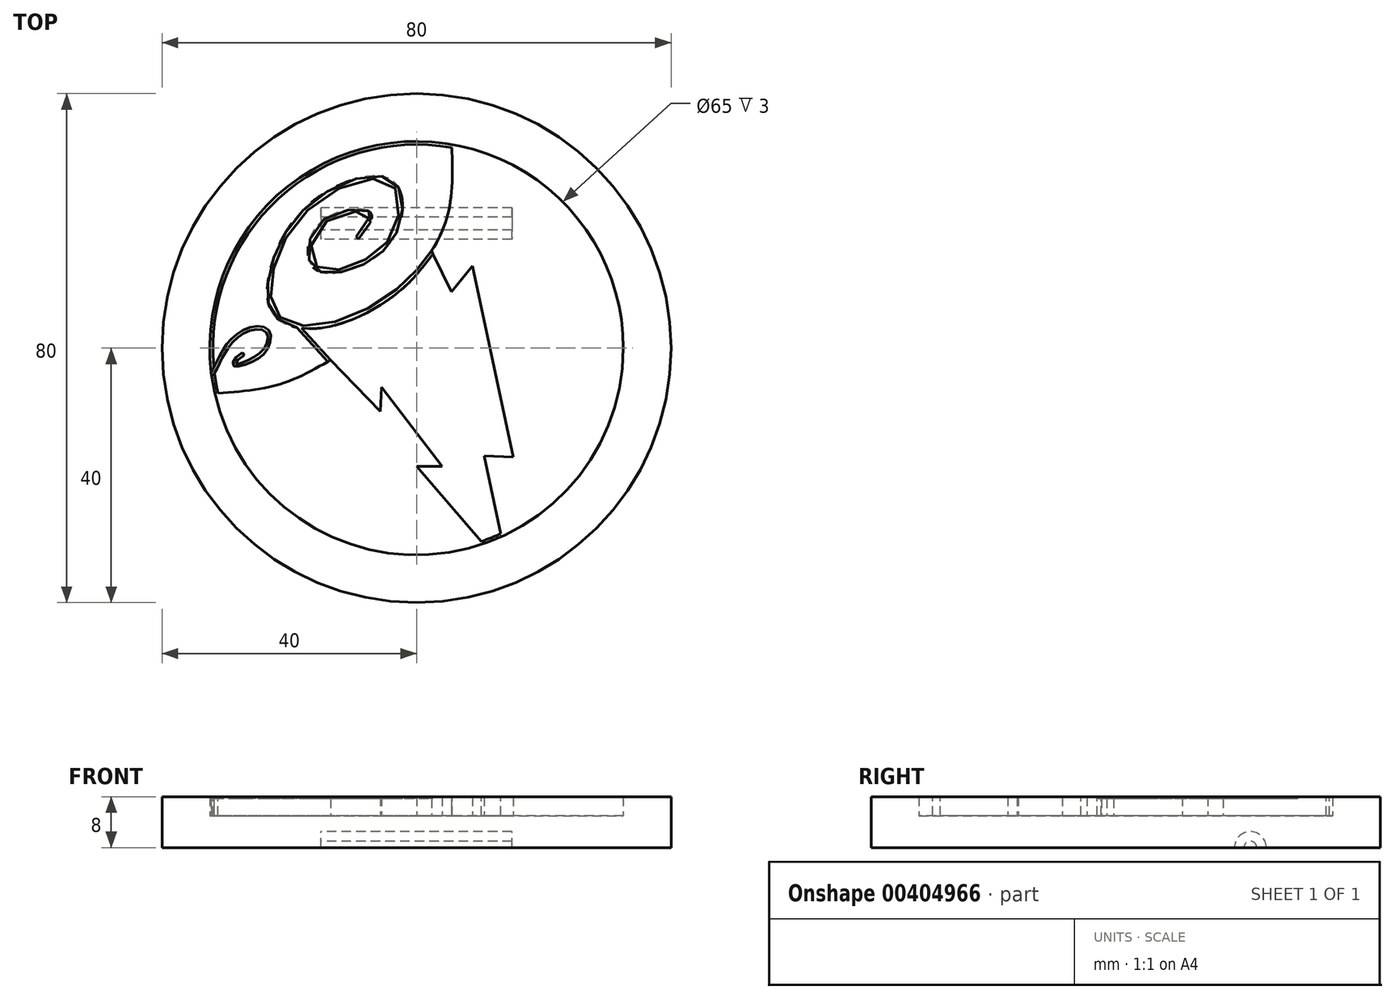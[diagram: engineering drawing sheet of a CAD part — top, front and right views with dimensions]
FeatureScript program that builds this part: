
annotation { "Feature Type Name" : "Feature", "Feature Type Description" : "" }
export const myFeature = defineFeature(function(context is Context, id is Id, definition is map)
    precondition{}
    {
        {
            var Q0;
            Q0=qCreatedBy(makeId("Top.planeOp"),FACE);
            var sketch = newSketch(context, id + "F0", { "sketchPlane" : qUnion([Q0])});
            skCircle(sketch, "E0", {"center": v(0, 0) * mm, "radius": 40 * mm});
            skSolve(sketch);
        }
        {
            var Q0;
            Q0=makeQuery(id+"F0.imprint","IMPRINT",FACE,{"disambiguationData":[TD([[makeQuery(id+"F0.imprint","IMPRINT",EDGE,{"derivedFrom":sQuery(id+"F0.wireOp",EDGE,"E0")}),1.0]])]});
            extrude(context, id + "F1", {"entities" : qUnion([Q0]), "depth" : 5 * mm});
        }
        {
            var Q0;
            Q0=makeQuery(id+"F1.opExtrude","CAP_FACE",FACE,{"disambiguationData":[OSD([sQuery(id+"F0.wireOp",EDGE,"E0")])],"isStart":false});
            var sketch = newSketch(context, id + "F2", { "sketchPlane" : qUnion([Q0])});
            skFitSpline(sketch, "E1", {"points": [v(5.4, 33.04) * mm, v(5.51, 24.72) * mm, v(3.5, 17.32) * mm, v(-2.5, 9.74) * mm, v(-14.12, 3.83) * mm, v(-22.3, 5.12) * mm, v(-23, 12.2) * mm, v(-15.9, 23.45) * mm, v(-4.33, 25.87) * mm, v(-3.61, 18.73) * mm, v(-9.95, 13.08) * mm, v(-16.28, 12.85) * mm, v(-13.76, 19.6) * mm, v(-7.69, 21.04) * mm, v(-9.52, 17.49) * mm], "startDerivative": vector(7.85, -74.03) * mm, "endDerivative": vector(-8.06, 0) * mm});
            skArc(sketch, "E2", {"start": v(10.84, -31.16) * mm, "mid": v(12.15, -30.67) * mm, "end": v(13.44, -30.13) * mm});
            skLineSegment(sketch, "E3", {"start": v(-13.5, -1.87) * mm, "end": v(-5.68, -9.95) * mm});
            skLineSegment(sketch, "E4", {"start": v(-5.68, -9.95) * mm, "end": v(-5.5, -6.12) * mm});
            skLineSegment(sketch, "E5", {"start": v(-5.5, -6.12) * mm, "end": v(4.02, -18.56) * mm});
            skLineSegment(sketch, "E6", {"start": v(4.02, -18.56) * mm, "end": v(0, -18.56) * mm});
            skLineSegment(sketch, "E7", {"start": v(0, -18.56) * mm, "end": v(10.84, -31.16) * mm});
            skLineSegment(sketch, "E8", {"start": v(2.36, 15.3) * mm, "end": v(5.49, 8.88) * mm});
            skLineSegment(sketch, "E9", {"start": v(5.49, 8.88) * mm, "end": v(8.77, 12.9) * mm});
            skLineSegment(sketch, "E10", {"start": v(8.77, 12.9) * mm, "end": v(15.17, -17.1) * mm});
            skLineSegment(sketch, "E11", {"start": v(15.17, -17.1) * mm, "end": v(10.6, -16.9) * mm});
            skLineSegment(sketch, "E12", {"start": v(10.6, -16.9) * mm, "end": v(13.44, -30.13) * mm});
            skFitSpline(sketch, "E13", {"points": [v(-32.21, -7.12) * mm, v(-21.77, -5.75) * mm, v(-13.5, -1.87) * mm], "startDerivative": vector(20.9, 1.22) * mm, "endDerivative": vector(16.44, 9.35) * mm});
            skArc(sketch, "E14.trimOffspring", {"start": v(5.44, 32.54) * mm, "mid": v(-23.92, 22.72) * mm, "end": v(-32.21, -7.12) * mm});
            skSolve(sketch);
        }
        {
            var Q0;
            Q0=qCreatedBy(makeId("Right.planeOp"),FACE);
            var Q1;
            Q1 = qBodyType(qCreatedBy(id + "F4" ,EDGE), BodyType.WIRE);
            cPlane(context, id + "F3", {"entities" : qUnion([Q0, Q1]), "cplaneType" : CPlaneType.OFFSET, "offset" : 15 * mm, "width" : 150 * mm, "height" : 150 * mm});
        }
        {
            var Q0;
            Q0=qCreatedBy(id+"F3.planeOp",FACE);
            var sketch = newSketch(context, id + "F4", { "sketchPlane" : qUnion([Q0])});
            skArc(sketch, "E15", {"start": v(22.09, 0) * mm, "mid": v(19.59, 2.5) * mm, "end": v(17.09, 0) * mm});
            skArc(sketch, "E16", {"start": v(20.59, 0) * mm, "mid": v(19.59, 1) * mm, "end": v(18.59, 0) * mm});
            skLineSegment(sketch, "E17", {"start": v(20.59, 0) * mm, "end": v(22.09, 0) * mm});
            skLineSegment(sketch, "E18", {"start": v(17.09, 0) * mm, "end": v(18.59, 0) * mm});
            skSolve(sketch);
        }
        {
            var Q0;
            Q0=qCreatedBy(makeId("Top.planeOp"),FACE);
            var sketch = newSketch(context, id + "F5", { "sketchPlane" : qUnion([Q0])});
            skLineSegment(sketch, "E19", {"start": v(15, 19.59) * mm, "end": v(-15, 19.59) * mm});
            skSolve(sketch);
        }
        {
            var Q0;
            Q0 = qSketchRegion(id + "F4", true);
            var Q1;
            Q1 = qSketchRegion(id + "F5", true);
            var Q2;
            Q2 = qConstructionFilter(qBodyType(qCreatedBy(id + "F5" ,EDGE), BodyType.WIRE), ConstructionObject.NO);
            sweep(context, id + "F6", {"operationType" : NewBodyOperationType.REMOVE, "profiles" : qUnion([Q0, Q1]), "path" : qUnion([Q2])});
        }
        {
            var Q0;
            Q0 = qSketchRegion(id + "F2", true);
            extrude(context, id + "F7", {"entities" : qUnion([Q0]), "operationType" : NewBodyOperationType.ADD, "depth" : 3 * mm});
        }
        {
            var Q0;
            Q0=makeQuery(id+"F7.opExtrude","CAP_FACE",FACE,{"disambiguationData":[OSD([sQuery(id+"F2.wireOp",EDGE,"E1"),sQuery(id+"F2.wireOp",EDGE,"E2"),sQuery(id+"F2.wireOp",EDGE,"E3"),sQuery(id+"F2.wireOp",EDGE,"E4"),sQuery(id+"F2.wireOp",EDGE,"E5"),sQuery(id+"F2.wireOp",EDGE,"E6"),sQuery(id+"F2.wireOp",EDGE,"E7"),sQuery(id+"F2.wireOp",EDGE,"E8"),sQuery(id+"F2.wireOp",EDGE,"E9"),sQuery(id+"F2.wireOp",EDGE,"E10"),sQuery(id+"F2.wireOp",EDGE,"E11"),sQuery(id+"F2.wireOp",EDGE,"E12"),sQuery(id+"F2.wireOp",EDGE,"E13"),sQuery(id+"F2.wireOp",EDGE,"E14.trimOffspring")])],"isStart":false});
            var sketch = newSketch(context, id + "F8", { "sketchPlane" : qUnion([Q0])});
            skFitSpline(sketch, "E20", {"points": [v(-32.67, -4.6) * mm, v(-31.03, -1.38) * mm, v(-29.23, 1.31) * mm, v(-25.82, 3.38) * mm, v(-23.13, 2.66) * mm, v(-23.6, -0.41) * mm, v(-26.36, -2.37) * mm, v(-28.78, -2.73) * mm, v(-27.35, -0.66) * mm], "startDerivative": vector(12.1, 24.07) * mm, "endDerivative": vector(32.58, 15.04) * mm});
            skFitSpline(sketch, "E21", {"points": [v(-32.6, -5.1) * mm, v(-31.7, -3.78) * mm, v(-30.58, -1.6) * mm, v(-28.88, 0.95) * mm, v(-25.74, 2.88) * mm, v(-23.52, 2.35) * mm, v(-23.94, -0.05) * mm, v(-26.53, -1.9) * mm, v(-28.34, -2.5) * mm, v(-27.09, -1.1) * mm], "startDerivative": vector(7.38, 14.23) * mm, "endDerivative": vector(32.67, 17.04) * mm});
            skLineSegment(sketch, "E22", {"start": v(-32.67, -4.6) * mm, "end": v(-32.6, -5.1) * mm});
            skLineSegment(sketch, "E23", {"start": v(-27.35, -0.66) * mm, "end": v(-27.09, -1.1) * mm});
            skSolve(sketch);
        }
        {
            var Q0;
            Q0 = qSketchRegion(id + "F8", true);
            extrude(context, id + "F9", {"entities" : qUnion([Q0]), "operationType" : NewBodyOperationType.REMOVE, "oppositeDirection" : true, "depth" : 0.3 * mm});
        }
        {
            var Q0;
            Q0=makeQuery(id+"F7.opExtrude","CAP_FACE",FACE,{"disambiguationData":[OSD([sQuery(id+"F2.wireOp",EDGE,"E1"),sQuery(id+"F2.wireOp",EDGE,"E2"),sQuery(id+"F2.wireOp",EDGE,"E3"),sQuery(id+"F2.wireOp",EDGE,"E4"),sQuery(id+"F2.wireOp",EDGE,"E5"),sQuery(id+"F2.wireOp",EDGE,"E6"),sQuery(id+"F2.wireOp",EDGE,"E7"),sQuery(id+"F2.wireOp",EDGE,"E8"),sQuery(id+"F2.wireOp",EDGE,"E9"),sQuery(id+"F2.wireOp",EDGE,"E10"),sQuery(id+"F2.wireOp",EDGE,"E11"),sQuery(id+"F2.wireOp",EDGE,"E12"),sQuery(id+"F2.wireOp",EDGE,"E13"),sQuery(id+"F2.wireOp",EDGE,"E14.trimOffspring")])],"isStart":false});
            var sketch = newSketch(context, id + "F10", { "sketchPlane" : qUnion([Q0])});
            skFitSpline(sketch, "E24", {"points": [v(2.36, 15.3) * mm, v(-2.5, 9.74) * mm, v(-14.2, 3.79) * mm, v(-21.82, 5.18) * mm, v(-22.51, 12.25) * mm, v(-15.51, 23.07) * mm, v(-4.16, 26) * mm, v(-3.5, 18.6) * mm, v(-9.91, 13.05) * mm, v(-15.9, 13.03) * mm, v(-14.8, 19.4) * mm, v(-7.66, 21.05) * mm, v(-9.51, 17.48) * mm], "startDerivative": vector(-50.55, -70.25) * mm, "endDerivative": vector(-63.63, -73.44) * mm});
            skLineSegment(sketch, "E25", {"start": v(2.36, 15.3) * mm, "end": v(2.58, 14.85) * mm});
            skLineSegment(sketch, "E26", {"start": v(-9.51, 17.48) * mm, "end": v(-9.14, 17.14) * mm});
            skFitSpline(sketch, "E27", {"points": [v(2.58, 14.85) * mm, v(-2.13, 9.41) * mm, v(-14.09, 3.3) * mm, v(-22.3, 5.04) * mm, v(-23.01, 12.25) * mm, v(-15.82, 23.46) * mm, v(-3.8, 26.35) * mm, v(-3.03, 18.42) * mm, v(-9.75, 12.57) * mm, v(-16.28, 12.71) * mm, v(-15.07, 19.83) * mm, v(-7.21, 21.27) * mm, v(-9.14, 17.14) * mm], "startDerivative": vector(-51.65, -69.05) * mm, "endDerivative": vector(-62.86, -74.96) * mm});
            skSolve(sketch);
        }
        {
            var Q0;
            Q0 = qSketchRegion(id + "F10", true);
            extrude(context, id + "F11", {"entities" : qUnion([Q0]), "operationType" : NewBodyOperationType.REMOVE, "oppositeDirection" : true, "depth" : 0.3 * mm});
        }
        {
            var Q0;
            Q0=makeQuery(id+"F7.opExtrude","CAP_FACE",FACE,{"disambiguationData":[OSD([sQuery(id+"F2.wireOp",EDGE,"E1"),sQuery(id+"F2.wireOp",EDGE,"E2"),sQuery(id+"F2.wireOp",EDGE,"E3"),sQuery(id+"F2.wireOp",EDGE,"E4"),sQuery(id+"F2.wireOp",EDGE,"E5"),sQuery(id+"F2.wireOp",EDGE,"E6"),sQuery(id+"F2.wireOp",EDGE,"E7"),sQuery(id+"F2.wireOp",EDGE,"E8"),sQuery(id+"F2.wireOp",EDGE,"E9"),sQuery(id+"F2.wireOp",EDGE,"E10"),sQuery(id+"F2.wireOp",EDGE,"E11"),sQuery(id+"F2.wireOp",EDGE,"E12"),sQuery(id+"F2.wireOp",EDGE,"E13"),sQuery(id+"F2.wireOp",EDGE,"E14.trimOffspring")])],"isStart":false});
            var sketch = newSketch(context, id + "F12", { "sketchPlane" : qUnion([Q0])});
            skLineSegment(sketch, "E28", {"start": v(-13.5, -1.87) * mm, "end": v(-18.05, 3.13) * mm});
            skLineSegment(sketch, "E29", {"start": v(-13.5, -1.87) * mm, "end": v(-13.93, -2.11) * mm});
            skLineSegment(sketch, "E30", {"start": v(-13.93, -2.11) * mm, "end": v(-18.82, 3.25) * mm});
            skLineSegment(sketch, "E31", {"start": v(-18.82, 3.25) * mm, "end": v(-18.05, 3.13) * mm});
            skSolve(sketch);
        }
        {
            var Q0;
            Q0 = qSketchRegion(id + "F12", true);
            extrude(context, id + "F13", {"entities" : qUnion([Q0]), "operationType" : NewBodyOperationType.REMOVE, "oppositeDirection" : true, "depth" : 0.3 * mm});
        }
        {
            var Q0;
            Q0=makeQuery(id+"F2.imprint","IMPRINT",FACE,{"disambiguationData":[TD([[makeQuery(id+"F2.imprint","IMPRINT",EDGE,{"derivedFrom":sQuery(id+"F2.wireOp",EDGE,"E1")}),1.0]])]});
            var sketch = newSketch(context, id + "F14", { "sketchPlane" : qUnion([Q0])});
            skCircle(sketch, "E32", {"center": v(0, 0) * mm, "radius": 40 * mm});
            skCircle(sketch, "E33", {"center": v(0, 0) * mm, "radius": 32.5 * mm});
            skSolve(sketch);
        }
        {
            var Q0;
            Q0 = qSketchRegion(id + "F14", true);
            extrude(context, id + "F15", {"entities" : qUnion([Q0]), "operationType" : NewBodyOperationType.ADD, "depth" : 3 * mm});
        }
        {
            var Q0;
            {var subQ0=sQuery(id+"F2.wireOp",EDGE,"E11");var subQ1=sQuery(id+"F2.wireOp",EDGE,"E10");var subQ2=sQuery(id+"F2.wireOp",EDGE,"E9");var subQ3=sQuery(id+"F2.wireOp",EDGE,"E8");var subQ4=sQuery(id+"F2.wireOp",EDGE,"E7");var subQ5=sQuery(id+"F2.wireOp",EDGE,"E6");var subQ6=sQuery(id+"F2.wireOp",EDGE,"E2");var subQ7=sQuery(id+"F2.wireOp",EDGE,"E3");var subQ8=sQuery(id+"F2.wireOp",EDGE,"E4");var subQ9=sQuery(id+"F2.wireOp",EDGE,"E5");var subQ10=sQuery(id+"F2.wireOp",EDGE,"E12");var subQ12=sQuery(id+"F2.wireOp",EDGE,"E14.trimOffspring");var subQ13=sQuery(id+"F2.wireOp",EDGE,"E13");var subQ14=sQuery(id+"F2.wireOp",EDGE,"E1");var subQ15=makeQuery(id+"F7.opExtrude","CAP_FACE",FACE,{"disambiguationData":[OSD([subQ14,subQ6,subQ7,subQ8,subQ9,subQ5,subQ4,subQ3,subQ2,subQ1,subQ0,subQ10,subQ13,subQ12])],"isStart":false});Q0=makeQuery(id+"F15.boolean.opBoolean","MERGE",FACE,{"derivedFrom":[makeQuery(id+"F13.boolean.opBoolean","SPLIT",FACE,{"disambiguationData":[TD([makeQuery(id+"F7.opExtrude","SWEPT_FACE",FACE,{"disambiguationData":[OSD([subQ14])]})])],"derivedFrom":subQ15}),makeQuery(id+"F13.boolean.opBoolean","SPLIT",FACE,{"disambiguationData":[TD([makeQuery(id+"F7.opExtrude","SWEPT_FACE",FACE,{"disambiguationData":[OSD([subQ6])]})])],"derivedFrom":subQ15}),makeQuery(id+"F15.opExtrude","CAP_FACE",FACE,{"disambiguationData":[OSD([sQuery(id+"F14.wireOp",EDGE,"E32"),sQuery(id+"F14.wireOp",EDGE,"E33")])],"isStart":false})]});}
            var sketch = newSketch(context, id + "F16", { "sketchPlane" : qUnion([Q0])});
            skArc(sketch, "E34", {"start": v(5.48, 32.03) * mm, "mid": v(-23.55, 22.4) * mm, "end": v(-31.72, -7.09) * mm});
            skLineSegment(sketch, "E35", {"start": v(-31.72, -7.09) * mm, "end": v(-31.22, -7.06) * mm});
            skLineSegment(sketch, "E36", {"start": v(5.48, 32.03) * mm, "end": v(5.52, 31.53) * mm});
            skArc(sketch, "E37", {"start": v(-31.22, -7.06) * mm, "mid": v(-23.18, 22.07) * mm, "end": v(5.52, 31.53) * mm});
            skLineSegment(sketch, "E38", {"start": v(10.5, -30.76) * mm, "end": v(10.17, -30.38) * mm});
            skLineSegment(sketch, "E39", {"start": v(13.34, -29.64) * mm, "end": v(13.24, -29.17) * mm});
            skArc(sketch, "E40", {"start": v(10.17, -30.38) * mm, "mid": v(11.72, -29.82) * mm, "end": v(13.24, -29.17) * mm});
            skArc(sketch, "E41", {"start": v(10.5, -30.76) * mm, "mid": v(11.93, -30.23) * mm, "end": v(13.34, -29.64) * mm});
            skSolve(sketch);
        }
        {
            var Q0;
            {var subQ6=sQuery(id+"F16.wireOp",EDGE,"E36");Q0=makeQuery(id+"F16.imprint","IMPRINT",FACE,{"disambiguationData":[TD([[makeQuery(id+"F16.imprint","IMPRINT",EDGE,{"derivedFrom":subQ6}),-1.0]])]});}
            var Q1;
            {var subQ3=sQuery(id+"F16.wireOp",EDGE,"E35");Q1=makeQuery(id+"F16.imprint","IMPRINT",FACE,{"disambiguationData":[TD([[makeQuery(id+"F16.imprint","IMPRINT",EDGE,{"derivedFrom":subQ3}),1.0]])]});}
            var Q2;
            Q2=makeQuery(id+"F16.imprint","IMPRINT",FACE,{"disambiguationData":[TD([[makeQuery(id+"F16.imprint","IMPRINT",EDGE,{"derivedFrom":sQuery(id+"F16.wireOp",EDGE,"E38")}),1.0]])]});
            extrude(context, id + "F17", {"entities" : qUnion([Q0, Q1, Q2]), "operationType" : NewBodyOperationType.REMOVE, "oppositeDirection" : true, "depth" : 3 * mm});
        }
    });
